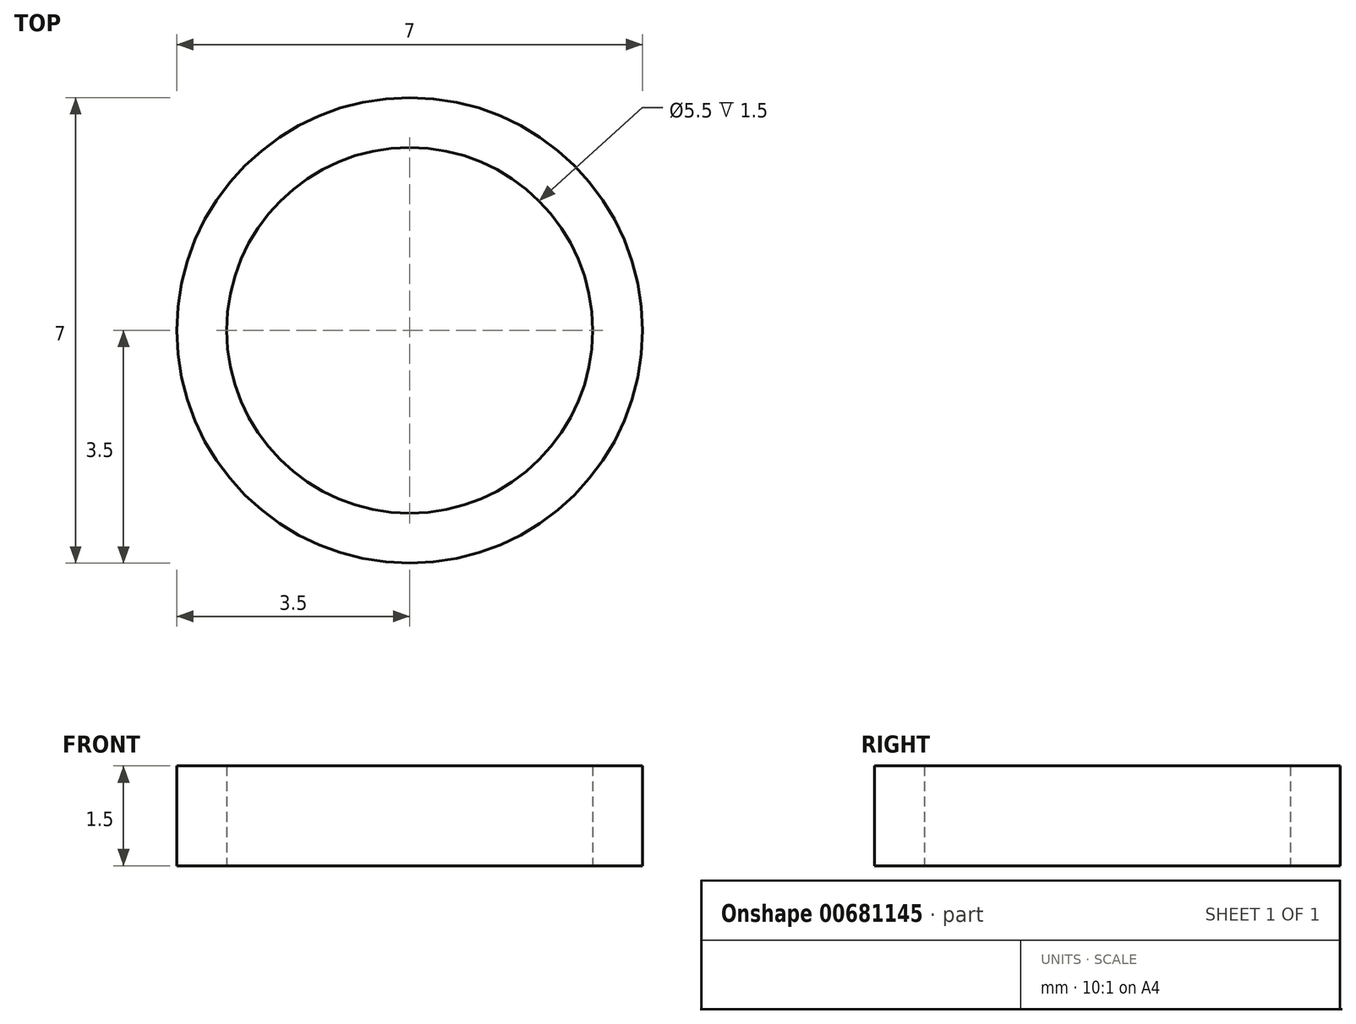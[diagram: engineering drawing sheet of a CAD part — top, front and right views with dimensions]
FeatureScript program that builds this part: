
annotation { "Feature Type Name" : "Feature", "Feature Type Description" : "" }
export const myFeature = defineFeature(function(context is Context, id is Id, definition is map)
    precondition{}
    {
        {
            var Q0;
            Q0=qCreatedBy(makeId("Top.planeOp"),FACE);
            var sketch = newSketch(context, id + "F0", { "sketchPlane" : qUnion([Q0])});
            skCircle(sketch, "E0", {"center": v(0, 0) * mm, "radius": 3.5 * mm});
            skCircle(sketch, "E1", {"center": v(0, 0) * mm, "radius": 2.75 * mm});
            skSolve(sketch);
        }
        {
            var Q0;
            Q0=makeQuery(id+"F0.imprint","IMPRINT",FACE,{"disambiguationData":[TD([[makeQuery(id+"F0.imprint","IMPRINT",EDGE,{"derivedFrom":sQuery(id+"F0.wireOp",EDGE,"E0")}),1.0]])]});
            extrude(context, id + "F1", {"entities" : qUnion([Q0]), "depth" : 1.5 * mm, "offsetDistance" : 25 * mm});
        }
    });
